# Revit family: KB311-SSWM_Closed
name_source: partatom
category: Specialty Equipment
revit_build: Autodesk Revit 2018 (Build: 20170223_1515(x64)
units: mm (PartAtom-declared; Revit-internal decimal feet)

## family parameters
Cut with Voids When Loaded = No
Host = Face
OmniClass Number = 23.40.20.21
OmniClass Title = Toilet and Bath Specialties
Part Type = Normal
Room Calculation Point = No
Round Connector Dimension = Use Diameter
Shared = Yes

## types (1)
- KB311-SSWM_Closed Position
    ADA Compliant = Yes
    ATS URL = http://www.atsspec.com
    Assembly Code = E2010
    Default Elevation = 24 7/16"
    Description = KB311-SSWM Baby Changing Station Closed Position
    Height = 41 15/32"
    Installation Type = Surace Mounted
    Length = 6 17/32"
    Manufacturer = Koala Kare
    Material = High Density Polyethylene- Koala Kare-Grey
    Model = KB311-SSWM
    Omniclass Table 23 Code = 23.40.20.21
    Omniclass Table 23 Title = Toilet and Bath Specialties
    Price = Prices may vary. Please consult Manufacturer Representative for most up-to-date price list.
    Product Documentation Link = https://f.hubspotusercontent20.net
    Product Page URL = https://info.koalabear.com
    Type Comments = Available Colors: Grey with Stainless Steel
    URL = http://www.koalabear.com
    Warranty Information = 5 Year Limited Warranty
    Width = 26 11/32"

## geometry (parser evidence)
native form markers: Sweep x8
no freeform markers — native parametric forms only
